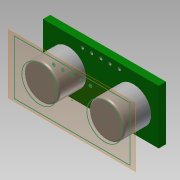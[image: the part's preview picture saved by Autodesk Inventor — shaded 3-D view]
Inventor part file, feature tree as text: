
AUTODESK INVENTOR PART (.ipt)
format: ipt  version: 2015 SP1 (Build 190203100, 203)  size: 146,432 bytes
history: native  units: mm
features: extrude x3, sketch x3, projected_geometry x2, fillet x1, plane x1
ambient origin geometry x8: Origin, YZ Plane, XZ Plane, XY Plane, X Axis, Y Axis, Z Axis, Center Point
bodies: Solid1 (feature_tree)
feature tree (10):
  extrude  "Extrusion1"  Depth=15.0mm
  sketch  "Sketch2"  dims[d4=2.0mm d5=0.0mm d8=9.8mm d11=32.0mm]
  extrude  "Extrusion3"  Depth=32.0mm
  fillet  "Fillet2"  Radius=32.0mm
  extrude  "Extrusion4"  Depth=7.4mm
  plane  "Work Plane1"
  sketch  "Sketch3"  dims[d12=15.0mm d16=8.0mm d17=9.8mm d19=9.0mm d20=9.0mm d21=7.4mm d22=0.0mm d23=0.5mm d24=0.8mm d25=1.44mm d26=0.8mm d27=2.54mm d28=0.8mm d29=2.54mm d30=7.4mm d31=0.0mm d32=8.0mm]
  sketch  "Sketch1"  dims[d0=32.0mm d1=15.0mm]
  projected_geometry  "Projected Loop1"
  projected_geometry  "Projected Loop2"
